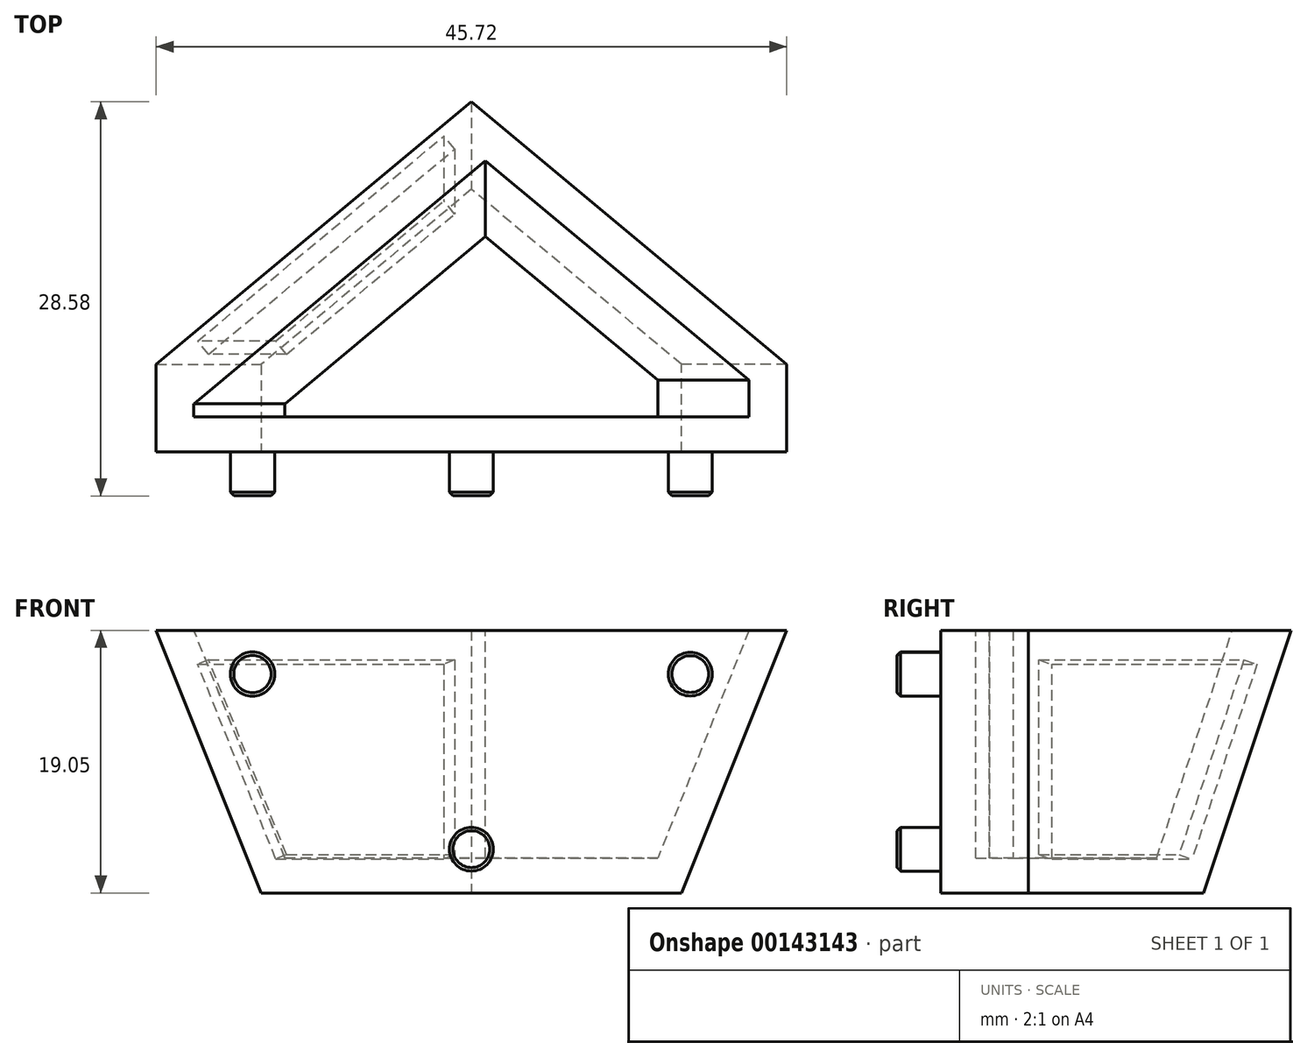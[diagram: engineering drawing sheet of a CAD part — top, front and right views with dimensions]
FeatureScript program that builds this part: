
annotation { "Feature Type Name" : "Feature", "Feature Type Description" : "" }
export const myFeature = defineFeature(function(context is Context, id is Id, definition is map)
    precondition{}
    {
        {
            var Q0;
            Q0=qCreatedBy(makeId("Top.planeOp"),FACE);
            var sketch = newSketch(context, id + "F0", { "sketchPlane" : qUnion([Q0])});
            skLineSegment(sketch, "E0", {"start": v(0, 0) * mm, "end": v(30.48, 0) * mm});
            skLineSegment(sketch, "E1", {"start": v(30.48, 0) * mm, "end": v(30.48, 6.35) * mm});
            skLineSegment(sketch, "E2", {"start": v(30.48, 6.35) * mm, "end": v(15.24, 19.05) * mm});
            skLineSegment(sketch, "E3", {"start": v(15.24, 19.05) * mm, "end": v(0, 6.35) * mm});
            skLineSegment(sketch, "E4", {"start": v(0, 6.35) * mm, "end": v(0, 0) * mm});
            skSolve(sketch);
        }
        {
            var Q0;
            Q0=qCreatedBy(makeId("Top.planeOp"),FACE);
            cPlane(context, id + "F1", {"entities" : qUnion([Q0]), "cplaneType" : CPlaneType.OFFSET, "offset" : 19.05 * mm, "width" : 152.4 * mm, "height" : 152.4 * mm});
        }
        {
            var Q0;
            Q0=qCreatedBy(id+"F1.planeOp",FACE);
            var sketch = newSketch(context, id + "F2", { "sketchPlane" : qUnion([Q0])});
            skLineSegment(sketch, "E5", {"start": v(-7.62, 0) * mm, "end": v(38.1, 0) * mm});
            skLineSegment(sketch, "E6", {"start": v(-7.62, 0) * mm, "end": v(-7.62, 6.35) * mm});
            skLineSegment(sketch, "E7", {"start": v(38.1, 0) * mm, "end": v(38.1, 6.35) * mm});
            skLineSegment(sketch, "E8", {"start": v(38.1, 6.35) * mm, "end": v(15.24, 25.4) * mm});
            skLineSegment(sketch, "E9", {"start": v(15.24, 25.4) * mm, "end": v(-7.62, 6.35) * mm});
            skSolve(sketch);
        }
        {
            var Q0;
            Q0=makeQuery(id+"F2.imprint","IMPRINT",FACE,{"disambiguationData":[TD([[makeQuery(id+"F2.imprint","IMPRINT",EDGE,{"derivedFrom":sQuery(id+"F2.wireOp",EDGE,"E5")}),1.0]])]});
            var Q1;
            Q1=makeQuery(id+"F0.imprint","IMPRINT",FACE,{"disambiguationData":[TD([[makeQuery(id+"F0.imprint","IMPRINT",EDGE,{"derivedFrom":sQuery(id+"F0.wireOp",EDGE,"E0")}),1.0]])]});
            loft(context, id + "F3", {"sheetProfilesArray" : [{ "sheetProfileEntities" : qUnion([Q0]) }, { "sheetProfileEntities" : qUnion([Q1]) }]});
        }
        {
            var Q0;
            Q0=makeQuery(id+"F3.opLoft","SWEPT_FACE",FACE,{"disambiguationData":[OSD([sQuery(id+"F0.wireOp",EDGE,"E2"),sQuery(id+"F0.wireOp",EDGE,"E3"),sQuery(id+"F0.wireOp",EDGE,"E4"),sQuery(id+"F2.wireOp",EDGE,"E6"),sQuery(id+"F2.wireOp",EDGE,"E8"),sQuery(id+"F2.wireOp",EDGE,"E9")])]});
            var sketch = newSketch(context, id + "F4", { "sketchPlane" : qUnion([Q0])});
            skLineSegment(sketch, "E10.0.0", {"start": v(-23.16, 26.1) * mm, "end": v(-23.16, 6.02) * mm});
            skLineSegment(sketch, "E10.0.1", {"start": v(-3.74, 2) * mm, "end": v(-23.16, 6.02) * mm});
            skLineSegment(sketch, "E10.0.2", {"start": v(-3.74, 2) * mm, "end": v(5.98, 20.08) * mm});
            skLineSegment(sketch, "E10.0.3", {"start": v(5.98, 20.08) * mm, "end": v(-23.16, 26.1) * mm});
            skLineSegment(sketch, "E11.0", {"start": v(-20.62, 22.99) * mm, "end": v(-20.62, 8.1) * mm});
            skLineSegment(sketch, "E11.1", {"start": v(2.13, 18.28) * mm, "end": v(-20.62, 22.99) * mm});
            skLineSegment(sketch, "E11.2", {"start": v(-5.08, 4.88) * mm, "end": v(2.13, 18.28) * mm});
            skLineSegment(sketch, "E11.3", {"start": v(-5.08, 4.88) * mm, "end": v(-20.62, 8.1) * mm});
            skSolve(sketch);
        }
        {
            var Q0;
            Q0=makeQuery(id+"F4.imprint","IMPRINT",FACE,{"disambiguationData":[TD([[makeQuery(id+"F4.imprint","IMPRINT",EDGE,{"derivedFrom":sQuery(id+"F4.wireOp",EDGE,"E11.0")}),1.0]])]});
            extrude(context, id + "F5", {"entities" : qUnion([Q0]), "operationType" : NewBodyOperationType.REMOVE, "oppositeDirection" : true, "depth" : 1.27 * mm});
        }
        {
            var Q0;
            Q0=qCreatedBy(makeId("Right.planeOp"),FACE);
            cPlane(context, id + "F6", {"entities" : qUnion([Q0]), "cplaneType" : CPlaneType.OFFSET, "offset" : 15.24 * mm, "width" : 152.4 * mm, "height" : 152.4 * mm});
        }
        {
            var Q0;
            Q0=makeQuery(id+"F3.opLoft","CAP_FACE",FACE,{"disambiguationData":[OSD([makeQuery(id+"F2.imprint","IMPRINT",FACE,{"disambiguationData":[TD([[makeQuery(id+"F2.imprint","IMPRINT",EDGE,{"derivedFrom":sQuery(id+"F2.wireOp",EDGE,"E5")}),1.0]])]})])],"isStart":true});
            shell(context, id + "F7", {"entities" : qUnion([Q0]), "thickness" : 2.54 * mm});
        }
        {
            var Q0;
            Q0=makeQuery(id+"F3.opLoft","SWEPT_FACE",FACE,{"disambiguationData":[OSD([sQuery(id+"F0.wireOp",EDGE,"E0"),sQuery(id+"F0.wireOp",EDGE,"E1"),sQuery(id+"F0.wireOp",EDGE,"E4"),sQuery(id+"F2.wireOp",EDGE,"E5"),sQuery(id+"F2.wireOp",EDGE,"E6"),sQuery(id+"F2.wireOp",EDGE,"E7")])]});
            var sketch = newSketch(context, id + "F8", { "sketchPlane" : qUnion([Q0])});
            skCircle(sketch, "E12", {"center": v(15.24, 3.18) * mm, "radius": 1.59 * mm});
            skCircle(sketch, "E13", {"center": v(-0.63, 15.88) * mm, "radius": 1.6 * mm});
            skCircle(sketch, "E14", {"center": v(31.12, 15.88) * mm, "radius": 1.59 * mm});
            skLineSegment(sketch, "E15.0.0", {"start": v(30.48, 0) * mm, "end": v(0, 0) * mm});
            skLineSegment(sketch, "E15.0.1", {"start": v(30.48, 0) * mm, "end": v(38.1, 19.05) * mm});
            skLineSegment(sketch, "E15.0.2", {"start": v(38.1, 19.05) * mm, "end": v(-7.62, 19.05) * mm});
            skLineSegment(sketch, "E15.0.3", {"start": v(-7.62, 19.05) * mm, "end": v(0, 0) * mm});
            skSolve(sketch);
        }
        {
            var Q0;
            Q0=makeQuery(id+"F8.imprint","IMPRINT",FACE,{"disambiguationData":[TD([[makeQuery(id+"F8.imprint","IMPRINT",EDGE,{"derivedFrom":sQuery(id+"F8.wireOp",EDGE,"E12")}),1.0]])]});
            var Q1;
            Q1=makeQuery(id+"F8.imprint","IMPRINT",FACE,{"disambiguationData":[TD([[makeQuery(id+"F8.imprint","IMPRINT",EDGE,{"derivedFrom":sQuery(id+"F8.wireOp",EDGE,"E14")}),1.0]])]});
            var Q2;
            Q2=makeQuery(id+"F8.imprint","IMPRINT",FACE,{"disambiguationData":[TD([[makeQuery(id+"F8.imprint","IMPRINT",EDGE,{"derivedFrom":sQuery(id+"F8.wireOp",EDGE,"E13")}),1.0]])]});
            extrude(context, id + "F9", {"entities" : qUnion([Q0, Q1, Q2]), "operationType" : NewBodyOperationType.ADD, "depth" : 3.17 * mm});
        }
        {
            var Q0;
            Q0=makeQuery(id+"F9.opExtrude","CAP_FACE",FACE,{"disambiguationData":[OSD([sQuery(id+"F8.wireOp",EDGE,"E13")])],"isStart":false});
            var Q1;
            Q1=makeQuery(id+"F9.opExtrude","CAP_FACE",FACE,{"disambiguationData":[OSD([sQuery(id+"F8.wireOp",EDGE,"E12")])],"isStart":false});
            var Q2;
            Q2=makeQuery(id+"F9.opExtrude","CAP_FACE",FACE,{"disambiguationData":[OSD([sQuery(id+"F8.wireOp",EDGE,"E14")])],"isStart":false});
            chamfer(context, id + "F10", {"entities" : qUnion([Q0, Q1, Q2]), "chamferType" : ChamferType.OFFSET_ANGLE, "width" : 0.25 * mm, "oppositeDirection" : false, "angle" : 45 * degree, "tangentPropagation" : true});
        }
    });
